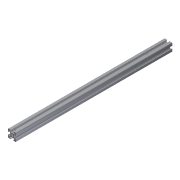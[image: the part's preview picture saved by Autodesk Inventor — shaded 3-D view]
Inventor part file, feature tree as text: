
AUTODESK INVENTOR PART (.ipt)
format: ipt  version: 2011 (Build 150239000, 239)  size: 394,752 bytes
history: native  units: in
note: dims shown in document units (in); Inventor stores cm internally (conversion verified against a paired STEP export)
features: plane x3, sketch x3, extrude x2, hole x1
ambient origin geometry x8: Origin, YZ Plane, XZ Plane, XY Plane, X Axis, Y Axis, Z Axis, Center Point
bodies: Solid1 (feature_tree)
feature tree (9):
  extrude  "Extrusion1"  TaperAngle=0.0deg  [1 undecoded]
  plane  "Work Plane2"
  plane  "Work Plane3"
  plane  "Work Plane4"
  hole  "Hole1"  [1 undecoded]
  extrude  "Extrusion3"  Depth=0.3937in
  sketch  "Sketch1"  dims[d0=15.9252in d1=0.0in d4=0.0in]
  sketch  "Sketch4"  dims[d5=0.0in d6=0.0in]
  sketch  "Sketch6"  dims[d7=0.9997in d8=0.3937in d9=15.9252in d10=7.9625in d11=2.0in d12=0.3937in d13=0.25in d14=0.75in d15=0.375in d16=0.25in d17=0.5635in d18=1.0in d19=0.8108in d22=0.6063in d23=0.0in d24=2.0in]
note: 2 required parameter values undecoded (feature->parameter linkage not recoverable at this tier; creation-order binding heuristic only, values carry confidence <= 0.55)
